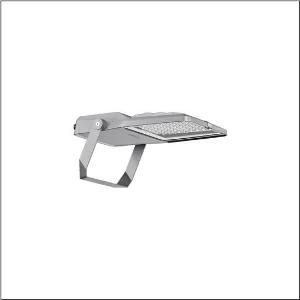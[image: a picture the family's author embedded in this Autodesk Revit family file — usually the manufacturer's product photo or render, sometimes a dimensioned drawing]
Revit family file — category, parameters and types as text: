
# Revit family: floodlight_fl_21_iq_mini___pl43_5xa7772c2a1a_250e
name_source: partatom
category: Lighting Fixtures
units: mm (PartAtom-declared; Revit-internal decimal feet)

## family parameters
Cut with Voids When Loaded = No
Host = Face
Light Source = No
Part Type = Normal
Room Calculation Point = No
Round Connector Dimension = Use Diameter
Shared = No

## types (1)
- --- (1 x LED, 12520 lm, 87.2 W, 3000K)
    Apparent Load = 87 VA
    CIE Flux Codes = 27 78 99 100 100
    Color Rendering = 70
    Color Temperature = 3000K
    Default Elevation = 1800 mm
    Description = Floodlight FL 21 iQ mini, floodlight, primary light control with lens, of PMMA, primary optical cover: protective disc, of toughened safety glass, transparent, light distribution: PL43, light emission: direct distribution, installation type: surface-mounted, LED, High Power LED, rated luminous flux: 12.520lm, luminous efficacy: 144lm/W, light colour: 730, colour temperature: 3000K, control: Street-Remote, Auto-Match, Temp-Guard, Night-Set, Smart-Wire, Desk-Remote (wireless, voltage-free reading and setting of iQ features in the workshop via application-optimized NFC function/RFID function), optimised constant luminous flux control (CLO 2.0), with terminal, 6-pole, mains connection: 220..240V, AC, 50/60Hz, start of lifetime: 87W, end of service life: 92W, reduction: 40W, luminaire housing, of diecast aluminium, powder-coated, Siteco® metallic grey (DB 702S), corrosivity category C5 mid according to DIN EN ISO 12944, sealing non-destructively replaceable, mounting bracket, of steel, galvanised, powder-coated, Siteco® metallic grey (DB 702S), protection rating (complete): IP66, insulation class (complete): insulation class II (safety insulation), certification: CE, ENEC, VDE, protection symbol: D, impact resistance: IK08, permissible operating ambient temperature: -40..+40°C, permissible operating ambient temperature for outdoor applications: -40..+50°C, standard: DIN EN 12944, LABS conformity tested according to VDMA 24364:2018-05, packaging unit: 1 piece

Light Distribution: PL43
    Height = 70 mm
    Lamp = 1 x LED
    Lamp Light Flux = 12520 lm
    Lamp Power = 87.2 W
    Lamp count = 1
    Length = 485 mm
    Luminous efficacy = 144 lm/W
    Manufacturer = Siteco
    ModVariant = No
    Model = 5XA7772C2A1A
    Number of Poles = 1
    OnlyDefault = Yes
    Power Factor = 1
    Product Name = Floodlight FL 21 iQ mini | PL43
    Product group = floodlight | pylon annexe
    ProductGroupID = 6200
    Protection Class = Protection class II
    Protection Degree = IP 66
    RLX_Detail_Level = 1
    RLX_Emergency_Light_Flux = 0 lm
    RLX_Emergency_Type = 0
    RLX_Emergency_Type_DB = No
    RlxData = <blob elided: 96173 chars, md5=cb3e4747>
    Socket = socket
    Standby Power = 0 W
    System Light Flux = 12520 lm
    System Power = 87 W
    Type Comments = factory setting: luminous flux: 100 % | dim-lin: 254 | 456 mA
    Type Image = l_1006845.jpg
    URL = http://relux.com
    VarID = @adj_094873
    Voltage = 0 V
    Weight = 0.00 kg
    Width = 337 mm

## geometry (parser evidence)
native form markers: Blend x4, Sweep x12
no freeform markers — native parametric forms only
